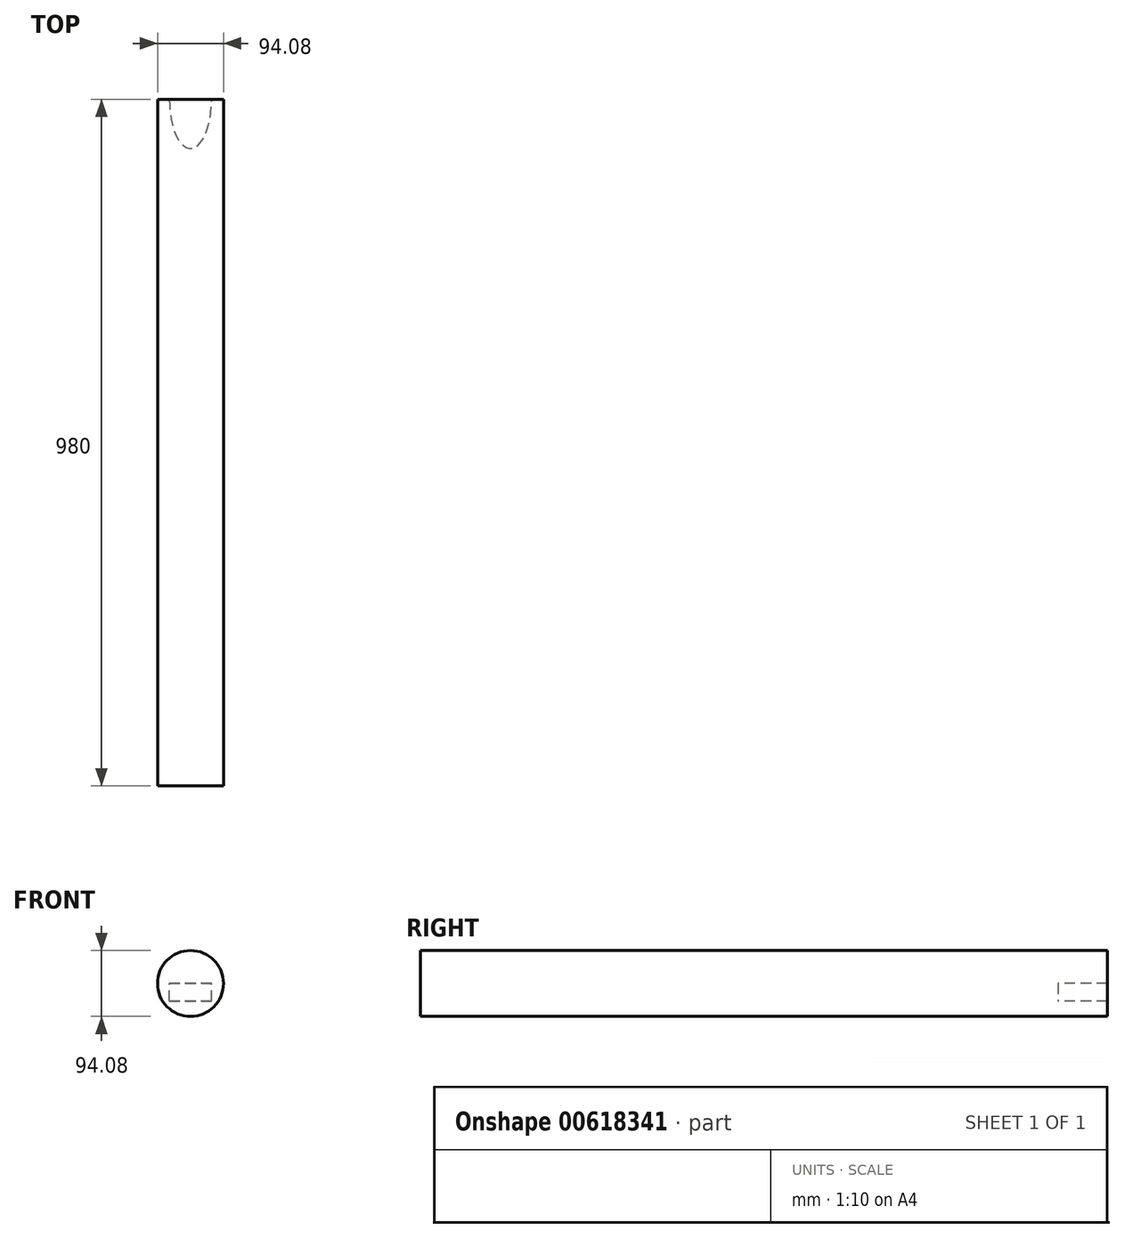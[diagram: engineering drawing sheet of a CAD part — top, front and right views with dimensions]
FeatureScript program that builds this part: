
annotation { "Feature Type Name" : "Feature", "Feature Type Description" : "" }
export const myFeature = defineFeature(function(context is Context, id is Id, definition is map)
    precondition{}
    {
        {
            var Q0;
            Q0=qCreatedBy(makeId("Front.planeOp"),FACE);
            var sketch = newSketch(context, id + "F0", { "sketchPlane" : qUnion([Q0])});
            skCircle(sketch, "E0", {"center": v(0, 0) * mm, "radius": 47.04 * mm});
            skSolve(sketch);
        }
        {
            var Q0;
            Q0=makeQuery(id+"F0.imprint","IMPRINT",FACE,{"disambiguationData":[TD([[makeQuery(id+"F0.imprint","IMPRINT",EDGE,{"derivedFrom":sQuery(id+"F0.wireOp",EDGE,"E0")}),1.0]])]});
            extrude(context, id + "F1", {"entities" : qUnion([Q0]), "depth" : 980 * mm, "offsetDistance" : 25 * mm});
        }
        {
            var Q0;
            Q0=qCreatedBy(makeId("Front.planeOp"),FACE);
            var sketch = newSketch(context, id + "F2", { "sketchPlane" : qUnion([Q0])});
            skCircle(sketch, "E1", {"center": v(0, 0) * mm, "radius": 25.75 * mm});
            skSolve(sketch);
        }
        {
            var Q0;
            Q0=makeQuery(id+"F2.imprint","IMPRINT",FACE,{"disambiguationData":[TD([[makeQuery(id+"F2.imprint","IMPRINT",EDGE,{"derivedFrom":sQuery(id+"F2.wireOp",EDGE,"E1")}),1.0]])]});
            extrude(context, id + "F3", {"entities" : qUnion([Q0]), "operationType" : NewBodyOperationType.ADD, "depth" : 25 * mm, "offsetDistance" : 25 * mm});
        }
        {
            var Q0;
            Q0=qCreatedBy(makeId("Top.planeOp"),FACE);
            var sketch = newSketch(context, id + "F4", { "sketchPlane" : qUnion([Q0])});
            skEllipse(sketch, "E2", {"center": v(0, 0) * mm, "majorRadius": 70.4 * mm, "minorRadius": 30.1 * mm, "majorAxis": v(0, 1)});
            skSolve(sketch);
        }
        {
            var Q0;
            Q0=makeQuery(id+"F4.imprint","IMPRINT",FACE,{"disambiguationData":[TD([[makeQuery(id+"F4.imprint","IMPRINT",EDGE,{"derivedFrom":sQuery(id+"F4.wireOp",EDGE,"E2")}),1.0]])]});
            extrude(context, id + "F5", {"entities" : qUnion([Q0]), "operationType" : NewBodyOperationType.REMOVE, "oppositeDirection" : true, "depth" : 25 * mm, "offsetDistance" : 25 * mm});
        }
    });
